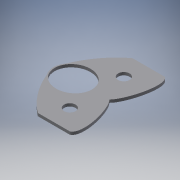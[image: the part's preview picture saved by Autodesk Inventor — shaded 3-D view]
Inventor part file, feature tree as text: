
AUTODESK INVENTOR PART (.ipt)
format: ipt  version: 2017 (Build 210142000, 142)  size: 117,760 bytes
history: native  units: mm
features: other x4, reference x2, extrude x1, sketch x1
ambient origin geometry x8: Origin, YZ Plane, XZ Plane, XY Plane, X Axis, Y Axis, Z Axis, Center Point
bodies: Body1 (feature_tree)
feature tree (8):
  other  "Bryła1"
  extrude  "Wyciągnięcie proste1"  Depth=1.0mm TaperAngle=0.0deg
  sketch  "Szkic1"
  reference  "Odniesienie1"
  reference  "Odniesienie2"
  other  "<userpath>\Desktop\quadrocopter rysunki\Zespół3.iam"
  other  "Zespół3.iam"
  other  "podwozie:1"
